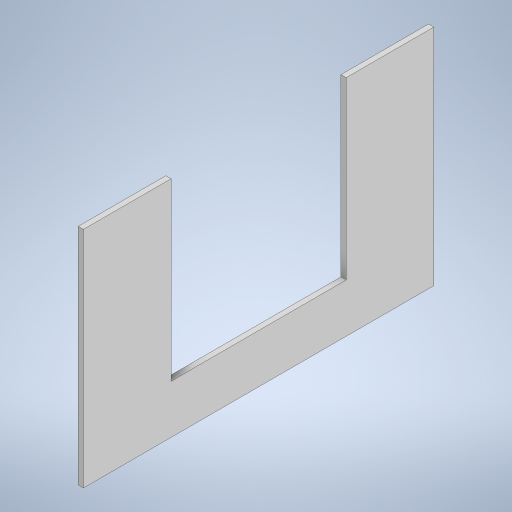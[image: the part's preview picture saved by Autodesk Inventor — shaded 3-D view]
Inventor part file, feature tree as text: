
AUTODESK INVENTOR PART (.ipt)
format: ipt  version: 2024.3 (Build 283343000, 343)  size: 217,088 bytes
history: native  units: mm
features: extrude x1, sketch x1
ambient origin geometry x8: Origin, YZ Plane, XZ Plane, XY Plane, X Axis, Y Axis, Z Axis, Center Point
bodies: Solid1 (feature_tree)
feature tree (2):
  extrude  "Extrusion1"  Depth=127.842mm
  sketch  "Sketch1"  dims[d0=200.0mm d1=127.842mm d2=100.0mm d3=100.0mm d4=50.0mm d5=3.0mm d6=0.0mm]
